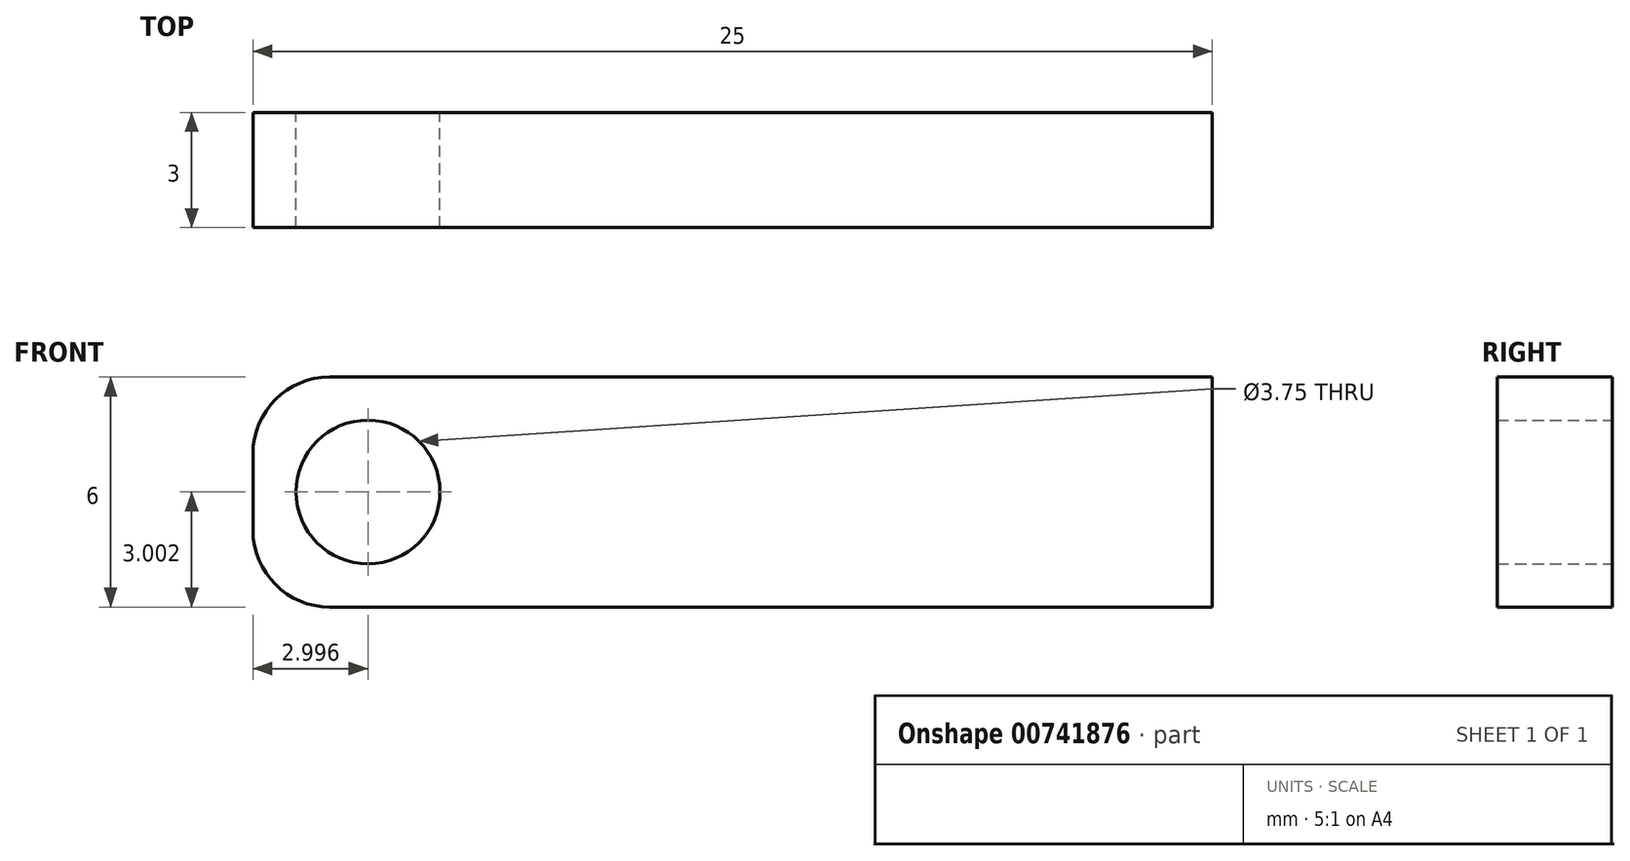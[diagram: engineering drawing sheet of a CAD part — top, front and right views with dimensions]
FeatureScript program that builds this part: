
annotation { "Feature Type Name" : "Feature", "Feature Type Description" : "" }
export const myFeature = defineFeature(function(context is Context, id is Id, definition is map)
    precondition{}
    {
        {
            var Q0;
            Q0=qCreatedBy(makeId("Front.planeOp"),FACE);
            var sketch = newSketch(context, id + "F0", { "sketchPlane" : qUnion([Q0])});
            skLineSegment(sketch, "E0.bottom", {"start": v(-35.6, 27.1) * mm, "end": v(-10.6, 27.1) * mm});
            skLineSegment(sketch, "E0.top", {"start": v(-35.6, 21.1) * mm, "end": v(-10.6, 21.1) * mm});
            skLineSegment(sketch, "E0.left", {"start": v(-35.6, 27.1) * mm, "end": v(-35.6, 21.1) * mm});
            skLineSegment(sketch, "E0.right", {"start": v(-10.6, 27.1) * mm, "end": v(-10.6, 21.1) * mm});
            skCircle(sketch, "E1", {"center": v(-32.6, 24.1) * mm, "radius": 1.88 * mm});
            skSolve(sketch);
        }
        {
            var Q0;
            Q0 = qSketchRegion(id + "F0", true);
            extrude(context, id + "F1", {"entities" : qUnion([Q0]), "depth" : 3 * mm, "offsetDistance" : 25 * mm});
        }
        {
            var Q0;
            Q0=makeQuery(id+"F1.opExtrude","SWEPT_EDGE",EDGE,{"disambiguationData":[OSD([sQuery(id+"F0.wireOp",EDGE,"E0.bottom"),sQuery(id+"F0.wireOp",EDGE,"E0.left")])]});
            var Q1;
            Q1=makeQuery(id+"F1.opExtrude","SWEPT_EDGE",EDGE,{"disambiguationData":[OSD([sQuery(id+"F0.wireOp",EDGE,"E0.top"),sQuery(id+"F0.wireOp",EDGE,"E0.left")])]});
            fillet(context, id + "F2", {"entities" : qUnion([Q0, Q1]), "radius" : 2 * mm, "tangentPropagation" : true, "allowEdgeOverflow" : false});
        }
    });
